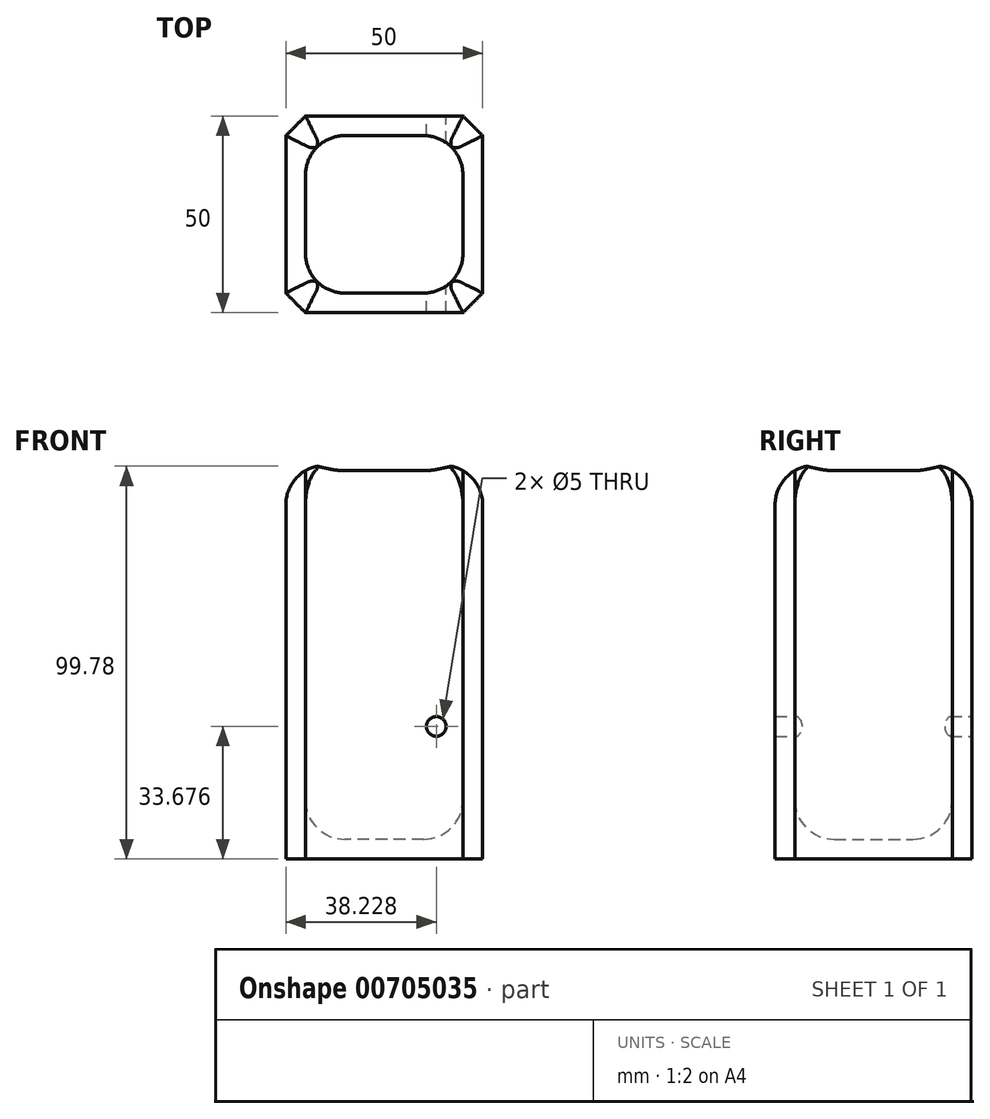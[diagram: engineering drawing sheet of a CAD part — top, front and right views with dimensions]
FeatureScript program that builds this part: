
annotation { "Feature Type Name" : "Feature", "Feature Type Description" : "" }
export const myFeature = defineFeature(function(context is Context, id is Id, definition is map)
    precondition{}
    {
        {
            var Q0;
            Q0=qCreatedBy(makeId("Top.planeOp"),FACE);
            var sketch = newSketch(context, id + "F0", { "sketchPlane" : qUnion([Q0])});
            skLineSegment(sketch, "E0.bottom", {"start": v(25, -25) * mm, "end": v(-25, -25) * mm});
            skLineSegment(sketch, "E0.top", {"start": v(25, 25) * mm, "end": v(-25, 25) * mm});
            skLineSegment(sketch, "E0.left", {"start": v(25, -25) * mm, "end": v(25, 25) * mm});
            skLineSegment(sketch, "E0.right", {"start": v(-25, -25) * mm, "end": v(-25, 25) * mm});
            skPoint(sketch, "E0.middle", {"position": v(0, 0) * mm});
            skSolve(sketch);
        }
        {
            var Q0;
            Q0 = qSketchRegion(id + "F0", true);
            extrude(context, id + "F1", {"entities" : qUnion([Q0]), "depth" : 100 * mm, "offsetDistance" : 25 * mm});
        }
        {
            var Q0;
            Q0=makeQuery(id+"F1.opExtrude","CAP_FACE",FACE,{"disambiguationData":[OSD([sQuery(id+"F0.wireOp",EDGE,"E0.bottom"),sQuery(id+"F0.wireOp",EDGE,"E0.top"),sQuery(id+"F0.wireOp",EDGE,"E0.left"),sQuery(id+"F0.wireOp",EDGE,"E0.right")])],"isStart":false});
            shell(context, id + "F2", {"entities" : qUnion([Q0]), "thickness" : 5 * mm});
        }
        {
            var Q0;
            Q0=makeQuery(id+"F1.opExtrude","CAP_EDGE",EDGE,{"disambiguationData":[OSD([sQuery(id+"F0.wireOp",EDGE,"E0.right")])],"isStart":false});
            var Q1;
            Q1=makeQuery(id+"F1.opExtrude","CAP_EDGE",EDGE,{"disambiguationData":[OSD([sQuery(id+"F0.wireOp",EDGE,"E0.top")])],"isStart":false});
            var Q2;
            Q2=makeQuery(id+"F1.opExtrude","CAP_EDGE",EDGE,{"disambiguationData":[OSD([sQuery(id+"F0.wireOp",EDGE,"E0.bottom")])],"isStart":false});
            var Q3;
            Q3=makeQuery(id+"F1.opExtrude","CAP_EDGE",EDGE,{"disambiguationData":[OSD([sQuery(id+"F0.wireOp",EDGE,"E0.left")])],"isStart":false});
            fillet(context, id + "F3", {"entities" : qUnion([Q0, Q1, Q2, Q3]), "radius" : 10 * mm, "tangentPropagation" : true, "allowEdgeOverflow" : false});
        }
        {
            var Q0;
            Q0=makeQuery(id+"F1.opExtrude","SWEPT_EDGE",EDGE,{"disambiguationData":[OSD([sQuery(id+"F0.wireOp",EDGE,"E0.bottom"),sQuery(id+"F0.wireOp",EDGE,"E0.left")])]});
            var Q1;
            Q1=makeQuery(id+"F1.opExtrude","SWEPT_EDGE",EDGE,{"disambiguationData":[OSD([sQuery(id+"F0.wireOp",EDGE,"E0.top"),sQuery(id+"F0.wireOp",EDGE,"E0.left")])]});
            var Q2;
            Q2=makeQuery(id+"F1.opExtrude","SWEPT_EDGE",EDGE,{"disambiguationData":[OSD([sQuery(id+"F0.wireOp",EDGE,"E0.top"),sQuery(id+"F0.wireOp",EDGE,"E0.right")])]});
            var Q3;
            Q3=makeQuery(id+"F1.opExtrude","SWEPT_EDGE",EDGE,{"disambiguationData":[OSD([sQuery(id+"F0.wireOp",EDGE,"E0.bottom"),sQuery(id+"F0.wireOp",EDGE,"E0.right")])]});
            chamfer(context, id + "F4", {"entities" : qUnion([Q0, Q1, Q2, Q3]), "width" : 5 * mm, "tangentPropagation" : true});
        }
        {
            var Q0;
            Q0=makeQuery(id+"F2.opShell","OFFSET_EDGE",EDGE,{"disambiguationData":[OSD([sQuery(id+"F0.wireOp",EDGE,"E0.top"),sQuery(id+"F0.wireOp",EDGE,"E0.left")])]});
            var Q1;
            {var subQ0=sQuery(id+"F0.wireOp",EDGE,"E0.left");Q1=makeQuery(id+"F2.opShell","OFFSET_EDGE",EDGE,{"disambiguationData":[OSD([subQ0]),TDD([makeQuery(id+"F1.opExtrude","CAP_EDGE",EDGE,{"disambiguationData":[OSD([subQ0])],"isStart":true})])]});}
            var Q2;
            {var subQ0=sQuery(id+"F0.wireOp",EDGE,"E0.top");Q2=makeQuery(id+"F2.opShell","OFFSET_EDGE",EDGE,{"disambiguationData":[OSD([subQ0]),TDD([makeQuery(id+"F1.opExtrude","CAP_EDGE",EDGE,{"disambiguationData":[OSD([subQ0])],"isStart":true})])]});}
            var Q3;
            Q3=makeQuery(id+"F2.opShell","OFFSET_EDGE",EDGE,{"disambiguationData":[OSD([sQuery(id+"F0.wireOp",EDGE,"E0.top"),sQuery(id+"F0.wireOp",EDGE,"E0.right")])]});
            var Q4;
            {var subQ0=sQuery(id+"F0.wireOp",EDGE,"E0.right");Q4=makeQuery(id+"F2.opShell","OFFSET_EDGE",EDGE,{"disambiguationData":[OSD([subQ0]),TDD([makeQuery(id+"F1.opExtrude","CAP_EDGE",EDGE,{"disambiguationData":[OSD([subQ0])],"isStart":true})])]});}
            var Q5;
            Q5=makeQuery(id+"F2.opShell","OFFSET_EDGE",EDGE,{"disambiguationData":[OSD([sQuery(id+"F0.wireOp",EDGE,"E0.bottom"),sQuery(id+"F0.wireOp",EDGE,"E0.right")])]});
            var Q6;
            {var subQ0=sQuery(id+"F0.wireOp",EDGE,"E0.bottom");Q6=makeQuery(id+"F2.opShell","OFFSET_EDGE",EDGE,{"disambiguationData":[OSD([subQ0]),TDD([makeQuery(id+"F1.opExtrude","CAP_EDGE",EDGE,{"disambiguationData":[OSD([subQ0])],"isStart":true})])]});}
            var Q7;
            Q7=makeQuery(id+"F2.opShell","OFFSET_EDGE",EDGE,{"disambiguationData":[OSD([sQuery(id+"F0.wireOp",EDGE,"E0.bottom"),sQuery(id+"F0.wireOp",EDGE,"E0.left")])]});
            fillet(context, id + "F5", {"entities" : qUnion([Q0, Q1, Q2, Q3, Q4, Q5, Q6, Q7]), "radius" : 10 * mm, "tangentPropagation" : true, "allowEdgeOverflow" : false});
        }
        {
            var Q0;
            Q0=makeQuery(id+"F1.opExtrude","SWEPT_FACE",FACE,{"disambiguationData":[OSD([sQuery(id+"F0.wireOp",EDGE,"E0.top")])]});
            var sketch = newSketch(context, id + "F6", { "sketchPlane" : qUnion([Q0])});
            skCircle(sketch, "E1", {"center": v(-13.23, 33.68) * mm, "radius": 2.74 * mm});
            skCircle(sketch, "E2", {"center": v(73.48, 36.2) * mm, "radius": 4.14 * mm});
            skSolve(sketch);
        }
        {
            var Q0;
            Q0=sQuery(id+"F6.wireOp",VERTEX,"E1.center");
            var Q1;
            Q1=makeQuery(id+"F1.opExtrude","SWEPT_BODY",BODY,{"disambiguationData":[OSD([sQuery(id+"F0.wireOp",EDGE,"E0.bottom"),sQuery(id+"F0.wireOp",EDGE,"E0.top"),sQuery(id+"F0.wireOp",EDGE,"E0.left"),sQuery(id+"F0.wireOp",EDGE,"E0.right")])]});
            hole(context, id + "F7", {"style" : HoleStyle.SIMPLE, "endStyle" : HoleEndStyle.THROUGH, "holeDiameter" : 5 * mm, "majorDiameter" : 5 * mm, "isTappedThrough" : true, "tappedDepth" : 12 * mm, "tapClearance" : 3, "locations" : qUnion([Q0]), "scope" : qUnion([Q1])});
        }
    });
